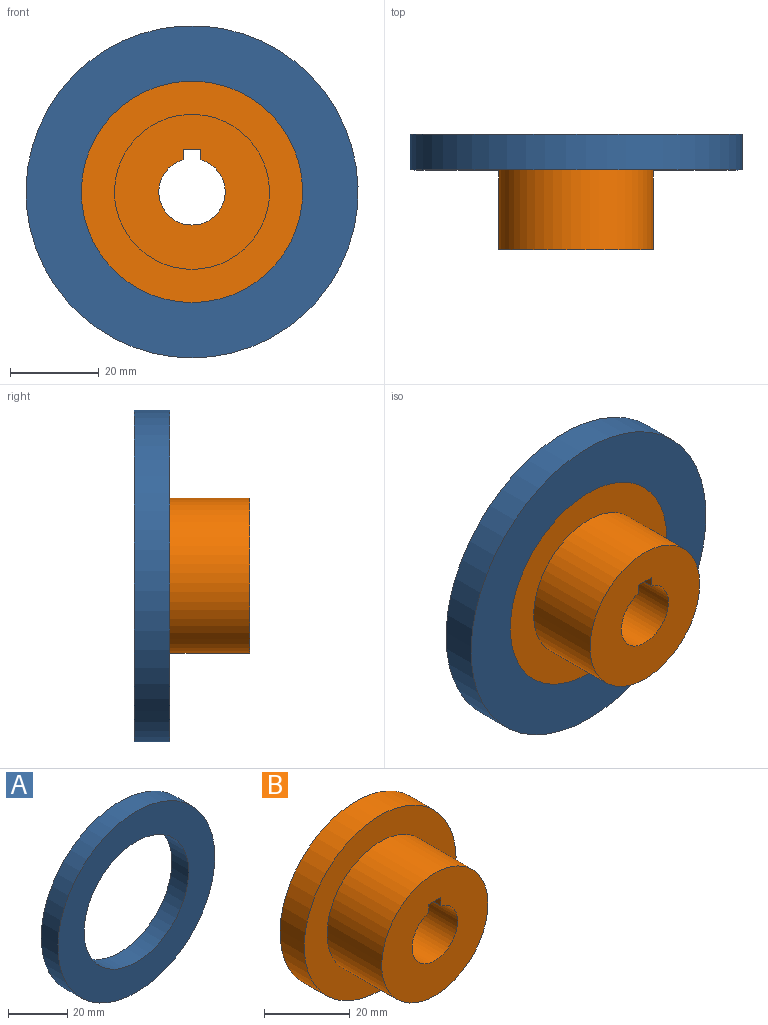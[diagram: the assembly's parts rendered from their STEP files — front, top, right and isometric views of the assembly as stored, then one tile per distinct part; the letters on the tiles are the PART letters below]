
ASSEMBLY  parts=2 mates=1
PART A: 4 faces, bbox 75x8x75 mm
  f0: cylinder r=25mm len=50mm, axis (0,1,0), area 1256.6mm2, adj f2,f3
  f1: cylinder r=37.5mm len=75mm, axis (0,1,0), area 1885mm2, adj f2,f3
  f2: plane 75x75mm, normal (0,-1,0), area 2454.4mm2, adj f0,f1
  f3: plane 75x75mm, normal (0,1,0), area 2454.4mm2, adj f0,f1
PART B: 9 faces, bbox 50x26x50 mm
  f0: plane 50x50mm, normal (0,1,0), area 1778.4mm2, adj f2,f5,f6,f7,f8
  f1: plane 35x35mm, normal (0,-1,0), area 777mm2, adj f4,f5,f6,f7,f8
  f2: cylinder r=25mm len=50mm, axis (0,1,0), area 1256.6mm2, adj f0,f3
  f3: plane 50x50mm, normal (0,-1,0), area 1001.4mm2, adj f2,f4
  f4: cylinder r=17.5mm len=35mm, axis (0,1,0), area 1979.2mm2, adj f1,f3
  f5: plane 26x2.27mm, normal (1,0,0), area 59.1mm2, adj f0,f1,f6,f8
  f6: cylinder r=7.5mm len=26mm, axis (0,-1,0), area 1119.9mm2, adj f0,f1,f5,f7
  f7: plane 26x2.27mm, normal (-1,0,0), area 59.1mm2, adj f0,f1,f6,f8
  f8: plane 26x4mm, normal (0,0,-1), area 104mm2, adj f0,f1,f5,f7
PLACE A t=(0.59,12.92,-0.64)mm
PLACE B t=(0.59,12.92,-0.64)mm fixed
MATE fastened A.f0 <-> B.f2  axis (0,-1,0) through (0.59,4.92,-0.64)mm
